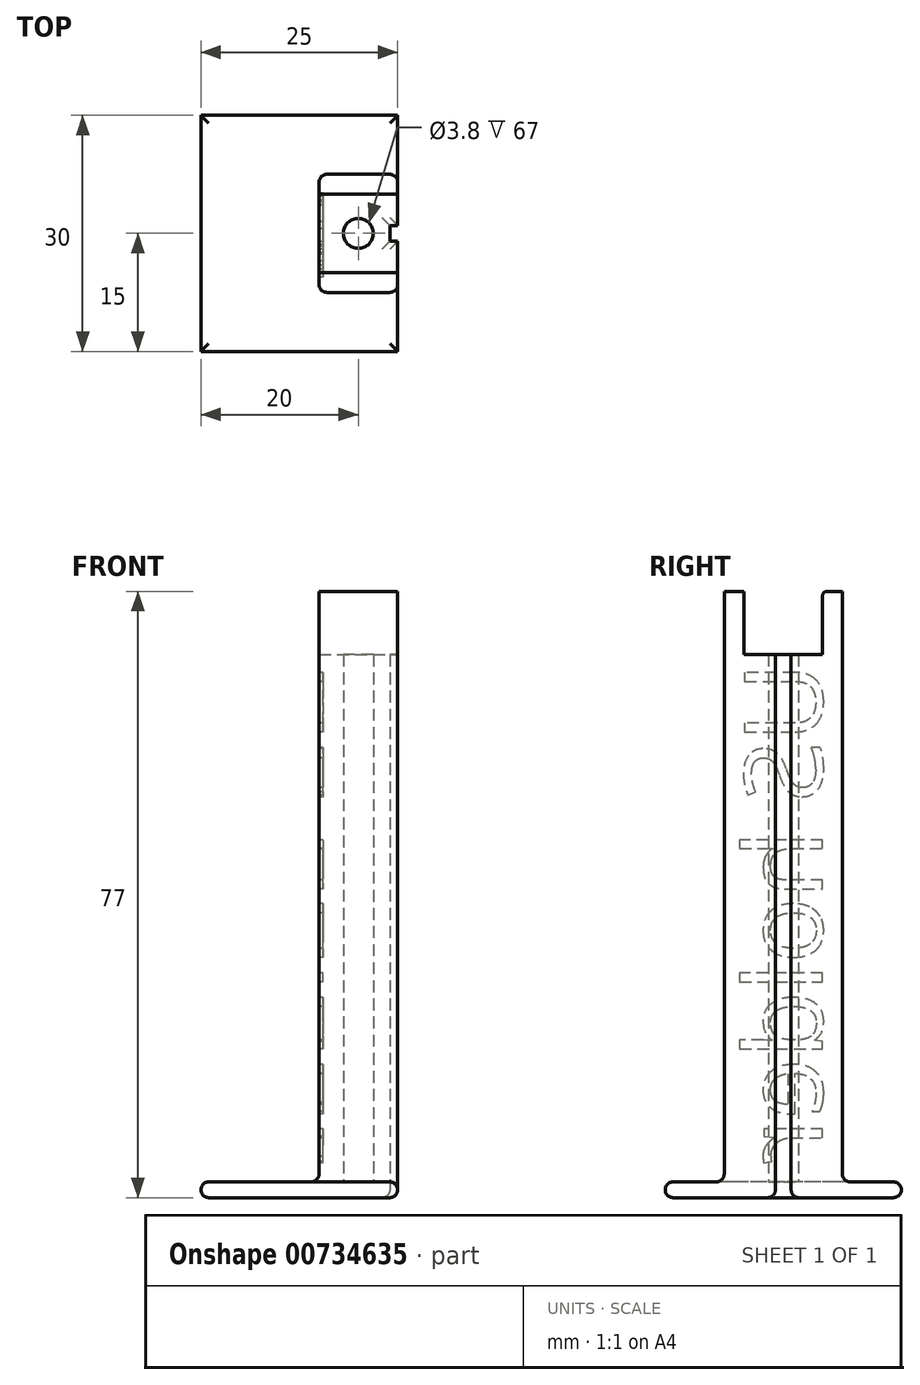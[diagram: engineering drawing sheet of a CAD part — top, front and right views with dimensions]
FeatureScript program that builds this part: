
annotation { "Feature Type Name" : "Feature", "Feature Type Description" : "" }
export const myFeature = defineFeature(function(context is Context, id is Id, definition is map)
    precondition{}
    {
        {
            var Q0;
            Q0=qCreatedBy(makeId("Top.planeOp"),FACE);
            var sketch = newSketch(context, id + "F0", { "sketchPlane" : qUnion([Q0])});
            skLineSegment(sketch, "E0.bottom", {"start": v(0, 15) * mm, "end": v(-25, 15) * mm});
            skLineSegment(sketch, "E0.top", {"start": v(0, -15) * mm, "end": v(-25, -15) * mm});
            skLineSegment(sketch, "E0.left", {"start": v(0, 15) * mm, "end": v(0, 1) * mm});
            skLineSegment(sketch, "E0.right", {"start": v(-25, 15) * mm, "end": v(-25, -15) * mm});
            skPoint(sketch, "E1.visualSharp", {"position": v(-25, 15) * mm});
            skLineSegment(sketch, "E1.filletArc", {"start": v(-25, 15) * mm, "end": v(-25, 15) * mm});
            skPoint(sketch, "E2.visualSharp", {"position": v(-25, -15) * mm});
            skLineSegment(sketch, "E2.filletArc", {"start": v(-25, -15) * mm, "end": v(-25, -15) * mm});
            skPoint(sketch, "E3.visualSharp", {"position": v(0, -15) * mm});
            skLineSegment(sketch, "E3.filletArc", {"start": v(0, -15) * mm, "end": v(0, -15) * mm});
            skPoint(sketch, "E4.visualSharp", {"position": v(0, 15) * mm});
            skLineSegment(sketch, "E4.filletArc", {"start": v(0, 15) * mm, "end": v(0, 15) * mm});
            skLineSegment(sketch, "E5.bottom", {"start": v(0, 1) * mm, "end": v(-1, 1) * mm});
            skLineSegment(sketch, "E5.top", {"start": v(0, -1) * mm, "end": v(-1, -1) * mm});
            skLineSegment(sketch, "E5.right", {"start": v(-1, 1) * mm, "end": v(-1, -1) * mm});
            skLineSegment(sketch, "E6.trimOffspring", {"start": v(0, -1) * mm, "end": v(0, -15) * mm});
            skSolve(sketch);
        }
        {
            var Q0;
            Q0 = qSketchRegion(id + "F0", true);
            extrude(context, id + "F1", {"entities" : qUnion([Q0]), "depth" : 2 * mm, "offsetDistance" : 25 * mm});
        }
        {
            var Q0;
            Q0=makeQuery(id+"F1.opExtrude","CAP_FACE",FACE,{"disambiguationData":[OSD([sQuery(id+"F0.wireOp",EDGE,"E0.bottom"),sQuery(id+"F0.wireOp",EDGE,"E0.top"),sQuery(id+"F0.wireOp",EDGE,"E0.left"),sQuery(id+"F0.wireOp",EDGE,"E0.right"),sQuery(id+"F0.wireOp",EDGE,"E1.filletArc"),sQuery(id+"F0.wireOp",EDGE,"E2.filletArc"),sQuery(id+"F0.wireOp",EDGE,"E3.filletArc"),sQuery(id+"F0.wireOp",EDGE,"E4.filletArc")])],"isStart":false});
            var sketch = newSketch(context, id + "F2", { "sketchPlane" : qUnion([Q0])});
            skLineSegment(sketch, "E7.bottom", {"start": v(0, 1) * mm, "end": v(-1, 1) * mm});
            skLineSegment(sketch, "E7.top", {"start": v(0, -1) * mm, "end": v(-1, -1) * mm});
            skLineSegment(sketch, "E7.right", {"start": v(-1, 1) * mm, "end": v(-1, -1) * mm});
            skCircle(sketch, "E8", {"center": v(-5, 0) * mm, "radius": 1.9 * mm});
            skLineSegment(sketch, "E9.bottom", {"start": v(0, 7.5) * mm, "end": v(-10, 7.5) * mm});
            skLineSegment(sketch, "E9.top", {"start": v(0, -7.5) * mm, "end": v(-10, -7.5) * mm});
            skLineSegment(sketch, "E9.left", {"start": v(0, 7.5) * mm, "end": v(0, 1) * mm});
            skLineSegment(sketch, "E9.right", {"start": v(-10, 7.5) * mm, "end": v(-10, -7.5) * mm});
            skLineSegment(sketch, "E10.trimOffspring", {"start": v(0, -1) * mm, "end": v(0, -7.5) * mm});
            skSolve(sketch);
        }
        {
            var Q0;
            Q0 = qSketchRegion(id + "F2", true);
            extrude(context, id + "F3", {"entities" : qUnion([Q0]), "operationType" : NewBodyOperationType.ADD, "depth" : 75 * mm, "offsetDistance" : 25 * mm});
        }
        {
            var Q0;
            Q0=makeQuery(id+"F3.opExtrude","CAP_FACE",FACE,{"disambiguationData":[OSD([sQuery(id+"F2.wireOp",EDGE,"E7.bottom"),sQuery(id+"F2.wireOp",EDGE,"E7.top"),sQuery(id+"F2.wireOp",EDGE,"E7.right"),sQuery(id+"F2.wireOp",EDGE,"E8"),sQuery(id+"F2.wireOp",EDGE,"E9.bottom"),sQuery(id+"F2.wireOp",EDGE,"E9.top"),sQuery(id+"F2.wireOp",EDGE,"E9.left"),sQuery(id+"F2.wireOp",EDGE,"E9.right"),sQuery(id+"F2.wireOp",EDGE,"E10.trimOffspring")])],"isStart":false});
            var sketch = newSketch(context, id + "F4", { "sketchPlane" : qUnion([Q0])});
            skLineSegment(sketch, "E11.bottom", {"start": v(-10, 5) * mm, "end": v(0, 5) * mm});
            skLineSegment(sketch, "E11.top", {"start": v(-10, -5) * mm, "end": v(0, -5) * mm});
            skLineSegment(sketch, "E11.left", {"start": v(-10, 5) * mm, "end": v(-10, -5) * mm});
            skLineSegment(sketch, "E11.right", {"start": v(0, 5) * mm, "end": v(0, -5) * mm});
            skSolve(sketch);
        }
        {
            var Q0;
            Q0 = qSketchRegion(id + "F4", true);
            extrude(context, id + "F5", {"entities" : qUnion([Q0]), "operationType" : NewBodyOperationType.REMOVE, "oppositeDirection" : true, "depth" : 8 * mm, "offsetDistance" : 25 * mm});
        }
        {
            var Q0;
            Q0=makeQuery(id+"F3.opExtrude","SWEPT_FACE",FACE,{"disambiguationData":[OSD([sQuery(id+"F2.wireOp",EDGE,"E9.right")])]});
            var sketch = newSketch(context, id + "F6", { "sketchPlane" : qUnion([Q0])});
            skText(sketch, "E12", { "text": "US holder", "fontName": "OpenSans-Regular.ttf"});
            const initialGuessF6  = {"E12": [-0.005, 0.068, 0, -1, 0.01]};
            skSetInitialGuess(sketch, initialGuessF6);
            skSolve(sketch);
        }
        {
            var Q0;
            Q0 = qSketchRegion(id + "F6", true);
            extrude(context, id + "F7", {"entities" : qUnion([Q0]), "operationType" : NewBodyOperationType.REMOVE, "oppositeDirection" : true, "depth" : 0.5 * mm, "offsetDistance" : 25 * mm});
        }
        {
            var Q0;
            Q0=makeQuery(id+"F3.opExtrude","SWEPT_EDGE",EDGE,{"disambiguationData":[OSD([sQuery(id+"F2.wireOp",EDGE,"E9.top"),sQuery(id+"F2.wireOp",EDGE,"E9.right")])]});
            var Q1;
            Q1=makeQuery(id+"F3.opExtrude","SWEPT_EDGE",EDGE,{"disambiguationData":[OSD([sQuery(id+"F0.wireOp",EDGE,"E6.trimOffspring"),sQuery(id+"F2.wireOp",EDGE,"E9.top"),sQuery(id+"F2.wireOp",EDGE,"E10.trimOffspring")])]});
            var Q2;
            Q2=makeQuery(id+"F3.opExtrude","SWEPT_EDGE",EDGE,{"disambiguationData":[OSD([sQuery(id+"F2.wireOp",EDGE,"E9.bottom"),sQuery(id+"F2.wireOp",EDGE,"E9.right")])]});
            var Q3;
            Q3=makeQuery(id+"F3.opExtrude","SWEPT_EDGE",EDGE,{"disambiguationData":[OSD([sQuery(id+"F0.wireOp",EDGE,"E0.left"),sQuery(id+"F2.wireOp",EDGE,"E9.bottom"),sQuery(id+"F2.wireOp",EDGE,"E9.left")])]});
            var Q4;
            {var subQ0=sQuery(id+"F0.wireOp",EDGE,"E0.left");var subQ1=sQuery(id+"F0.wireOp",EDGE,"E0.top");var subQ2=sQuery(id+"F0.wireOp",EDGE,"E0.right");var subQ3=sQuery(id+"F0.wireOp",EDGE,"E0.bottom");var subQ4=sQuery(id+"F0.wireOp",EDGE,"E6.trimOffspring");Q4=makeQuery(id+"F3.boolean.opBoolean","SPLIT",FACE,{"disambiguationData":[TD([makeQuery(id+"F1.opExtrude","SWEPT_FACE",FACE,{"disambiguationData":[OSD([subQ3])]})])],"derivedFrom":makeQuery(id+"F1.opExtrude","CAP_FACE",FACE,{"disambiguationData":[OSD([subQ3,subQ1,subQ0,subQ2,sQuery(id+"F0.wireOp",EDGE,"E5.bottom"),sQuery(id+"F0.wireOp",EDGE,"E5.top"),sQuery(id+"F0.wireOp",EDGE,"E5.right"),subQ4])],"isStart":false})});}
            var Q5;
            Q5=makeQuery(id+"F1.opExtrude","CAP_FACE",FACE,{"disambiguationData":[OSD([sQuery(id+"F0.wireOp",EDGE,"E0.bottom"),sQuery(id+"F0.wireOp",EDGE,"E0.top"),sQuery(id+"F0.wireOp",EDGE,"E0.left"),sQuery(id+"F0.wireOp",EDGE,"E0.right"),sQuery(id+"F0.wireOp",EDGE,"E5.bottom"),sQuery(id+"F0.wireOp",EDGE,"E5.top"),sQuery(id+"F0.wireOp",EDGE,"E5.right"),sQuery(id+"F0.wireOp",EDGE,"E6.trimOffspring")])],"isStart":true});
            fillet(context, id + "F8", {"entities" : qUnion([Q0, Q1, Q2, Q3, Q4, Q5]), "tangentPropagation" : true, "radius" : 1 * mm, "defaultsChanged" : false, "vertexSettings" : [], "allowEdgeOverflow" : false});
        }
        {
            var Q0;
            Q0=makeQuery(id+"F5.boolean.opBoolean","COPY",EDGE,{"derivedFrom":makeQuery(id+"F5.opExtrude","CAP_EDGE",EDGE,{"disambiguationData":[OSD([sQuery(id+"F4.wireOp",EDGE,"E11.bottom")])],"isStart":true})});
            var Q1;
            Q1=makeQuery(id+"F5.boolean.opBoolean","COPY",EDGE,{"derivedFrom":makeQuery(id+"F5.opExtrude","CAP_EDGE",EDGE,{"disambiguationData":[OSD([sQuery(id+"F4.wireOp",EDGE,"E11.top")])],"isStart":true})});
            fillet(context, id + "F9", {"entities" : qUnion([Q0, Q1]), "tangentPropagation" : true, "radius" : 0.5 * mm, "defaultsChanged" : false, "vertexSettings" : [], "allowEdgeOverflow" : false});
        }
    });
